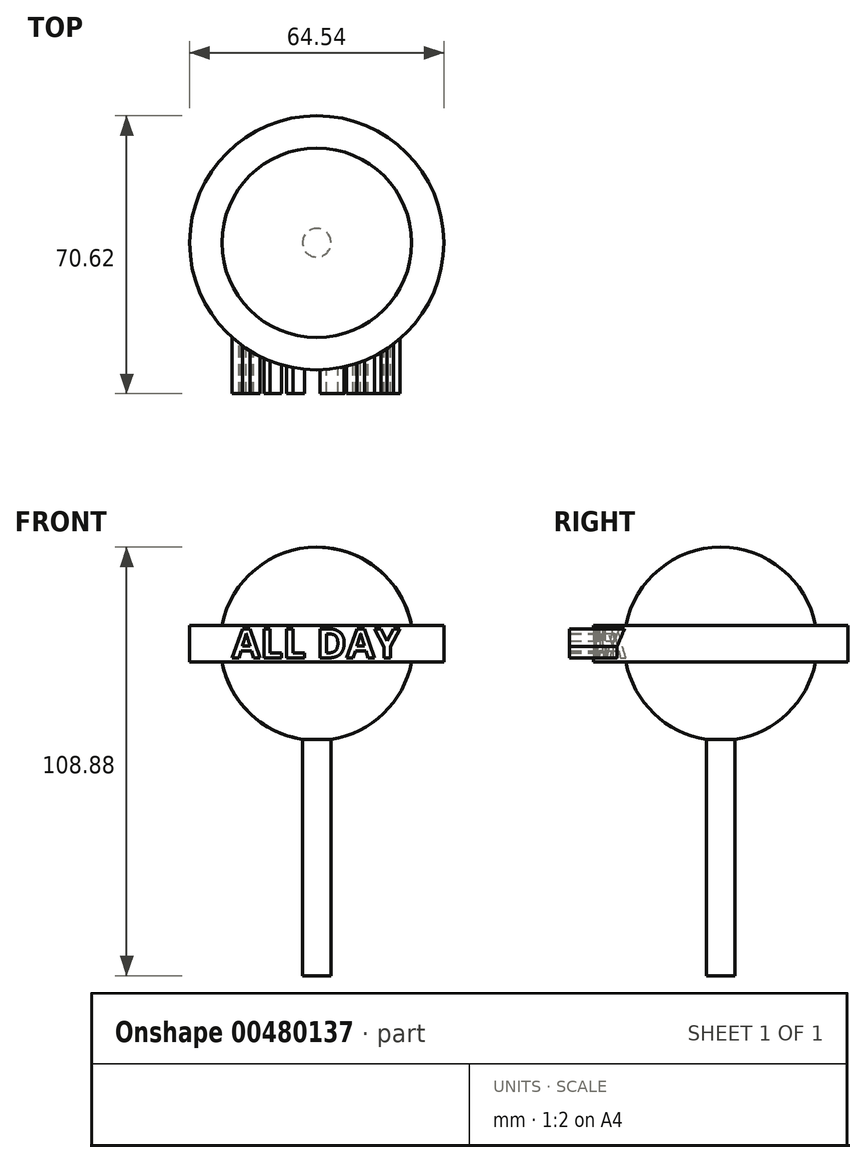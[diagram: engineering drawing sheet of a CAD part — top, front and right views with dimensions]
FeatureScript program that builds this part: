
annotation { "Feature Type Name" : "Feature", "Feature Type Description" : "" }
export const myFeature = defineFeature(function(context is Context, id is Id, definition is map)
    precondition{}
    {
        {
            var Q0;
            Q0=qCreatedBy(makeId("Front.planeOp"),FACE);
            var sketch = newSketch(context, id + "F0", { "sketchPlane" : qUnion([Q0])});
            skArc(sketch, "E0", {"start": v(0, -24.53) * mm, "mid": v(24.53, 0) * mm, "end": v(0, 24.53) * mm});
            skLineSegment(sketch, "E1", {"start": v(0, 24.53) * mm, "end": v(0, -24.53) * mm});
            skPoint(sketch, "E2.orphan", {"position": v(0, 28.21) * mm});
            skLineSegment(sketch, "E3", {"start": v(0, -24.53) * mm, "end": v(0, 58.88) * mm, "construction": true});
            skLineSegment(sketch, "E4.bottom", {"start": v(12.97, -4.65) * mm, "end": v(36.08, -4.65) * mm});
            skLineSegment(sketch, "E4.top", {"start": v(12.97, 4.65) * mm, "end": v(36.08, 4.65) * mm});
            skLineSegment(sketch, "E4.left", {"start": v(12.97, -4.65) * mm, "end": v(12.97, 4.65) * mm});
            skLineSegment(sketch, "E4.right", {"start": v(32.27, -4.65) * mm, "end": v(32.27, 4.65) * mm});
            skPoint(sketch, "E4.middle", {"position": v(24.53, 0) * mm});
            skLineSegment(sketch, "E5.bottom", {"start": v(0, -20.88) * mm, "end": v(3.62, -20.88) * mm});
            skLineSegment(sketch, "E5.top", {"start": v(0, -84.35) * mm, "end": v(3.62, -84.35) * mm});
            skLineSegment(sketch, "E5.left", {"start": v(0, -20.88) * mm, "end": v(0, -84.35) * mm});
            skLineSegment(sketch, "E5.right", {"start": v(3.62, -20.88) * mm, "end": v(3.62, -84.35) * mm});
            skSolve(sketch);
        }
        {
            var Q0;
            Q0 = qSketchRegion(id + "F0", true);
            var Q1;
            Q1=sQuery(id+"F0.wireOp",EDGE,"E3");
            revolve(context, id + "F1", {"entities" : qUnion([Q0]), "axis" : qUnion([Q1]), "revolveType" : RevolveType.FULL});
        }
        {
            var Q0;
            Q0=qCreatedBy(makeId("Front.planeOp"),FACE);
            var sketch = newSketch(context, id + "F2", { "sketchPlane" : qUnion([Q0])});
            skText(sketch, "E6", { "text": "ALL DAY", "fontName": "OpenSans-Bold.ttf"});
            const initialGuessF2  = {"E6": [-0.02148, -0.00359, 1, 0, 0.00742]};
            skSetInitialGuess(sketch, initialGuessF2);
            skSolve(sketch);
        }
        {
            var Q0;
            Q0 = qSketchRegion(id + "F2", true);
            extrude(context, id + "F3", {"entities" : qUnion([Q0]), "operationType" : NewBodyOperationType.ADD, "depth" : 38.35 * mm, "offsetDistance" : 25.4 * mm});
        }
    });
